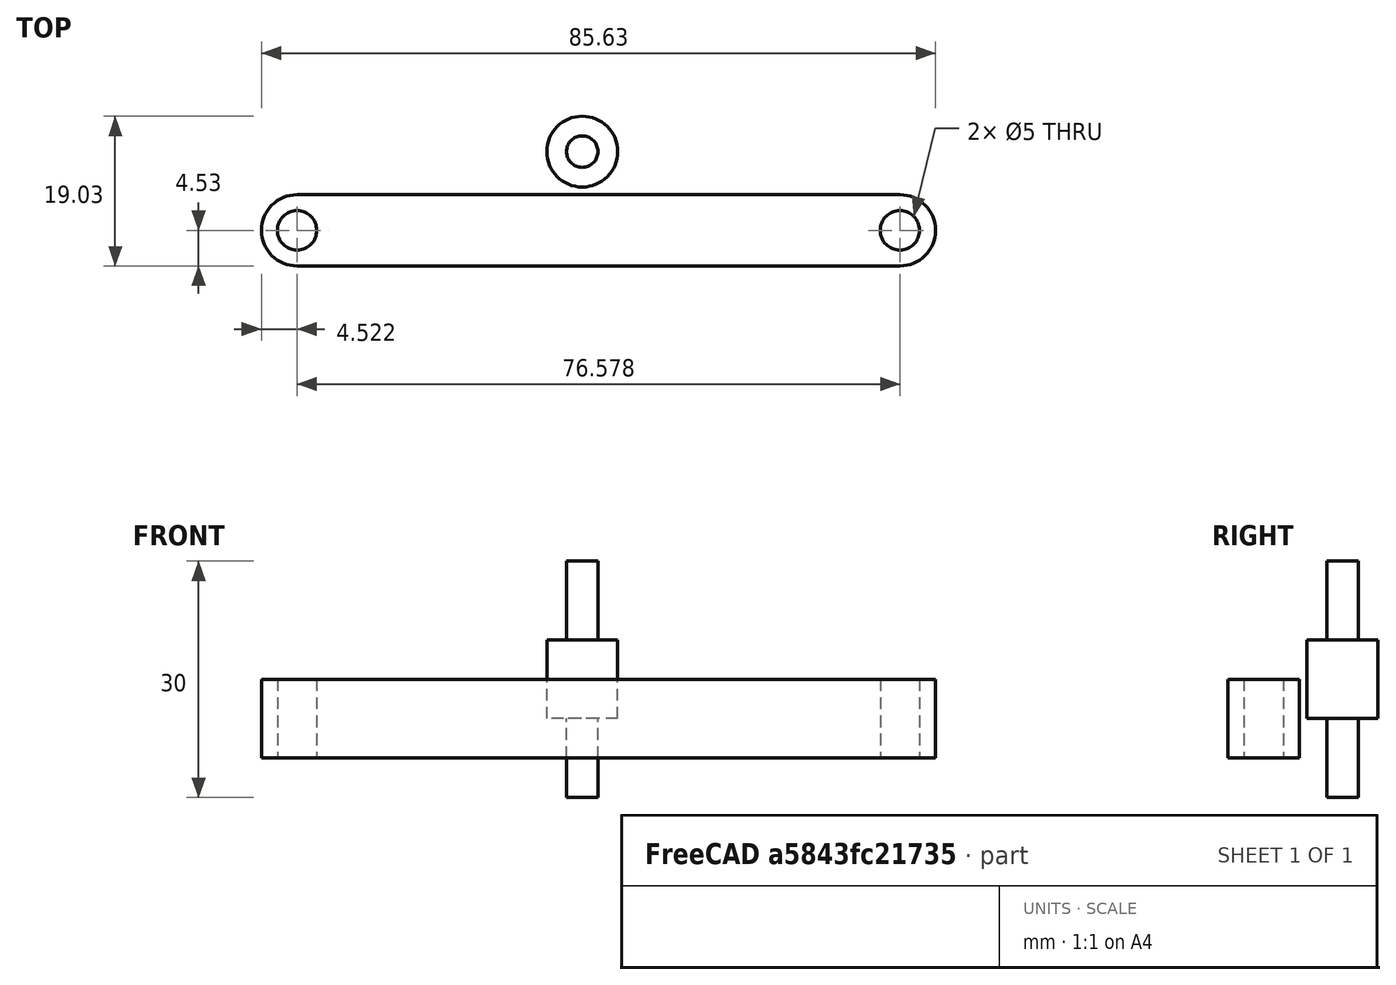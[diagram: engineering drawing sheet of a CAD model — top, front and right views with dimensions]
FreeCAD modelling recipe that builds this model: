
FCSTD DOCUMENT  (FreeCAD 0.19R24291 (Git))
Label: FBR_defLink
License: All rights reserved
LicenseURL: http://en.wikipedia.org/wiki/All_rights_reserved
objects: Part::Cylinder×2, Sketcher::SketchObject×1, PartDesign::Pad×1, PartDesign::Hole×1, PartDesign::Body×1, Part::MultiFuse×1, App::MeasureDistance×1
note: 9 computed .brp shape members not serialized (recipe doc carries the construction recipe); baked Part::Feature solids carry a one-line shape summary decoded from their .brp

FEATURE [Sketcher::SketchObject] Sketch
  FullyConstrained = false
  MapMode = 5
  Support = -> [XY_Plane]
  sketch-geometry (4):
    g0: ArcOfCircle CenterX=-36.2276 CenterY=0 CenterZ=0 NormalX=0 NormalY=0 NormalZ=1 AngleXU=0 Radius=4.52517 StartAngle=1.5708 EndAngle=4.71239
    g1: ArcOfCircle CenterX=40.3501 CenterY=4e-16 CenterZ=0 NormalX=0 NormalY=0 NormalZ=1 AngleXU=0 Radius=4.52517 StartAngle=4.71239 EndAngle=7.85398
    g2: LineSegment StartX=-36.2276 StartY=-4.52517 StartZ=0 EndX=40.3501 EndY=-4.52517 EndZ=0
    g3: LineSegment StartX=-36.2276 StartY=4.52517 StartZ=0 EndX=40.3501 EndY=4.52517 EndZ=0
  constraints (7):
    c: Tangent(g0,g3) = 1.5708
    c: Tangent(g0,g2) = -1.5708
    c: Tangent(g2,g1) = -1.5708
    c: Tangent(g3,g1) = 1.5708
    c: Horizontal(g2)
    c: Equal(g0,g1)
    c: PointOnObject(g0,g-1)
FEATURE [PartDesign::Pad] Pad
  Direction = (1,1,1)
  Length = 10
  Length2 = 100
  Profile = -> Sketch
  Type = 0
FEATURE [PartDesign::Hole] Hole
  BaseFeature = -> Pad
  Depth = 25
  DepthType = 0
  Diameter = 5
  DrillForDepth = false
  DrillPoint = 1
  DrillPointAngle = 118
  HoleCutCountersinkAngle = 90
  HoleCutCustomValues = false
  HoleCutDepth = 0
  HoleCutDiameter = 6.1
  HoleCutType = 0
  ModelActualThread = false
  Profile = -> Pad [Face6]
  Tapered = false
  TaperedAngle = 90
  ThreadAngle = 0
  ThreadClass = 0
  ThreadCutOffInner = 0
  ThreadCutOffOuter = 0
  ThreadDirection = 0
  ThreadFit = 0
  ThreadPitch = 0
  ThreadSize = 0
  ThreadType = 0
  Threaded = false
FEATURE [PartDesign::Body] Body  label="def_Link"
  Group = -> [Sketch,Pad,Hole]
  Origin = -> Origin
  Tip = -> Hole
FEATURE [Part::Cylinder] Cylinder
  Angle = 360
  AttacherType = Attacher::AttachEngine3D
  Height = 30
  Placement = pos=(0,10,-5) rot=(0,0,1;0rad)
  Radius = 2
FEATURE [Part::Cylinder] Cylinder001
  Angle = 360
  AttacherType = Attacher::AttachEngine3D
  Height = 10
  Placement = pos=(0,10,5) rot=(0,0,1;0rad)
  Radius = 4.5
FEATURE [Part::MultiFuse] Fusion
  Shapes = -> [Cylinder,Cylinder001]
FEATURE [App::MeasureDistance] Distance002  label="Distance: 10,00 mm"
  Distance = 10.0002
  P1 = (20.0464,4.52517,0)
  P2 = (19.9776,4.52517,10)
